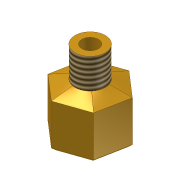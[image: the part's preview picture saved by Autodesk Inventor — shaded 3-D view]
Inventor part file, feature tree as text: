
AUTODESK INVENTOR PART (.ipt)
format: ipt  version: unknown  size: 217,600 bytes
history: native  units: mm (DEFAULTED — no unit token found)
features: sketch x5, extrude x4, thread x2, plane x1, loft x1, chamfer x1, projected_geometry x1
ambient origin geometry x8: Origin, YZ Plane, XZ Plane, XY Plane, X Axis, Y Axis, Z Axis, Center Point
feature tree (15):
  extrude  "Extrusion1"  Depth=14.478mm TaperAngle=0.0deg
  plane  "Work Plane1"
  sketch  "Sketch2"  dims[d3=2.032mm d4=10.0mm]
  loft  "Loft1"
  extrude  "Extrusion2"  TaperAngle=0.0deg  [1 undecoded]
  extrude  "Extrusion3"  Depth=11.5mm
  extrude  "Extrusion4"  Depth=5.5mm
  thread  "Thread1"  [1 undecoded]
  thread  "Thread2"  [1 undecoded]
  chamfer  "Chamfer1"  [1 undecoded]
  sketch  "Sketch1"  dims[d0=19.05mm d1=14.478mm d2=0.0mm]
  sketch  "Sketch3"  dims[d5=0.0mm d6=90.0deg d7=0.0mm d8=90.0deg]
  projected_geometry  "Projected Loop1"
  sketch  "Sketch4"  dims[d9=10.0mm d10=0.0mm d11=11.5mm]
  sketch  "Sketch5"  dims[d12=11.75mm d13=0.0mm d14=5.5mm d15=19.0mm d16=0.0mm d17=10.0mm d18=0.0mm d19=10.0mm d20=0.0mm d21=1.0mm d22=2.0mm d23=45.0deg]
note: 4 required parameter values undecoded (feature->parameter linkage not recoverable at this tier; creation-order binding heuristic only, values carry confidence <= 0.55)
